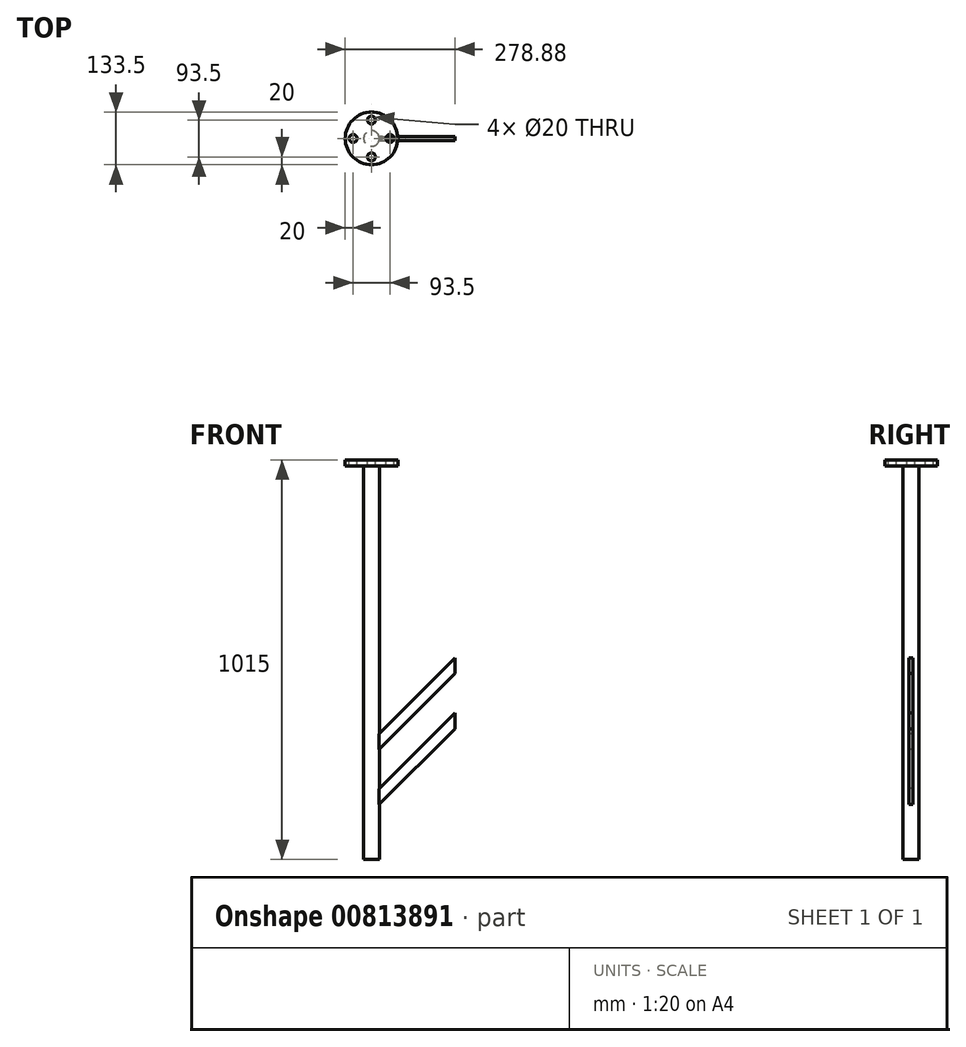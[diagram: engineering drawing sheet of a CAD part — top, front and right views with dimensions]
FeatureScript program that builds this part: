
annotation { "Feature Type Name" : "Feature", "Feature Type Description" : "" }
export const myFeature = defineFeature(function(context is Context, id is Id, definition is map)
    precondition{}
    {
        {
            var Q0;
            Q0=qCreatedBy(makeId("Top.planeOp"),FACE);
            var sketch = newSketch(context, id + "F0", { "sketchPlane" : qUnion([Q0])});
            skCircle(sketch, "E0", {"center": v(0, 0) * mm, "radius": 66.75 * mm});
            skSolve(sketch);
        }
        {
            var Q0;
            Q0 = qSketchRegion(id + "F0", true);
            extrude(context, id + "F1", {"entities" : qUnion([Q0]), "depth" : 15 * mm, "offsetDistance" : 25.4 * mm});
        }
        {
            var Q0;
            Q0=makeQuery(id+"F1.opExtrude","CAP_FACE",FACE,{"disambiguationData":[OSD([sQuery(id+"F0.wireOp",EDGE,"E0")])],"isStart":true});
            var sketch = newSketch(context, id + "F2", { "sketchPlane" : qUnion([Q0])});
            skCircle(sketch, "E1", {"center": v(0, 0) * mm, "radius": 20 * mm});
            skSolve(sketch);
        }
        {
            var Q0;
            Q0 = qSketchRegion(id + "F2", true);
            extrude(context, id + "F3", {"entities" : qUnion([Q0]), "operationType" : NewBodyOperationType.ADD, "depth" : 1000 * mm, "offsetDistance" : 25.4 * mm});
        }
        {
            var Q0;
            Q0=qCreatedBy(makeId("Front.planeOp"),FACE);
            var sketch = newSketch(context, id + "F4", { "sketchPlane" : qUnion([Q0])});
            skLineSegment(sketch, "E2", {"start": v(0, -700) * mm, "end": v(212.13, -487.87) * mm});
            skLineSegment(sketch, "E3", {"start": v(212.13, -487.87) * mm, "end": v(212.13, -527.87) * mm});
            skLineSegment(sketch, "E4", {"start": v(212.13, -527.87) * mm, "end": v(0, -740) * mm});
            skLineSegment(sketch, "E5", {"start": v(0, -700) * mm, "end": v(0, -740) * mm});
            skLineSegment(sketch, "E6", {"start": v(0, -840) * mm, "end": v(0, -880) * mm});
            skLineSegment(sketch, "E7", {"start": v(0, -880) * mm, "end": v(212.13, -667.87) * mm});
            skLineSegment(sketch, "E8", {"start": v(212.13, -667.87) * mm, "end": v(212.13, -627.87) * mm});
            skLineSegment(sketch, "E9", {"start": v(212.13, -627.87) * mm, "end": v(0, -840) * mm});
            skSolve(sketch);
        }
        {
            var Q0;
            Q0 = qSketchRegion(id + "F4", true);
            extrude(context, id + "F5", {"entities" : qUnion([Q0]), "operationType" : NewBodyOperationType.ADD, "endBound" : BoundingType.SYMMETRIC, "depth" : 10 * mm, "offsetDistance" : 25.4 * mm});
        }
        {
            var Q0;
            Q0=makeQuery(id+"F1.opExtrude","CAP_FACE",FACE,{"disambiguationData":[OSD([sQuery(id+"F0.wireOp",EDGE,"E0")])],"isStart":false});
            var sketch = newSketch(context, id + "F6", { "sketchPlane" : qUnion([Q0])});
            skCircle(sketch, "E10", {"center": v(0, 0) * mm, "radius": 46.75 * mm, "construction": true});
            skCircle(sketch, "E11", {"center": v(0, -46.75) * mm, "radius": 10 * mm});
            skCircle(sketch, "E12.1.1", {"center": v(46.75, 0) * mm, "radius": 10 * mm});
            skCircle(sketch, "E12.2.1", {"center": v(0, 46.75) * mm, "radius": 10 * mm});
            skCircle(sketch, "E12.3.1", {"center": v(-46.75, 0) * mm, "radius": 10 * mm});
            skSolve(sketch);
        }
        {
            var Q0;
            Q0 = qSketchRegion(id + "F6", true);
            extrude(context, id + "F7", {"entities" : qUnion([Q0]), "operationType" : NewBodyOperationType.REMOVE, "oppositeDirection" : true, "depth" : 50.8 * mm, "offsetDistance" : 25.4 * mm});
        }
    });
